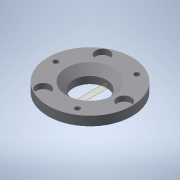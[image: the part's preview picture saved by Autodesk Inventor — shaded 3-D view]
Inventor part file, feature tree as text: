
AUTODESK INVENTOR PART (.ipt)
format: ipt  version: 2022 (Build 260153000, 153)  size: 187,392 bytes
history: native  units: mm
features: reference x5, sketch x4, extrude x2, other x2, plane x1, revolve x1, hole x1
ambient origin geometry x8: Origin, YZ Plane, XZ Plane, XY Plane, X Axis, Y Axis, Z Axis, Center Point
bodies: Volumenkörper1 (feature_tree)
feature tree (16):
  plane  "Arbeitsebene1"
  revolve  "Umdrehung1"
  hole  "Bohrung1"  [1 undecoded]
  extrude  "Extrusion1"  Depth=4.0mm
  extrude  "Extrusion2"  Depth=1.3mm
  sketch  "Skizze1"  dims[d0=3.0mm d1=12.0mm]
  reference  "Referenz1"
  reference  "Referenz2"
  sketch  "Skizze2"  dims[d4=4.0mm d5=4.0mm]
  reference  "Referenz3"
  reference  "Referenz4"
  reference  "Referenz5"
  sketch  "Skizze3"  dims[d6=1.0mm d7=1.3mm]
  sketch  "Skizze4"  dims[d8=2.6mm d9=90.0deg d10=4.0mm d11=0.2mm d13=2.9mm d14=6.0mm d15=6.0mm d16=3.0mm d17=90.0deg d18=12.0mm d19=20.594885mm d20=0.0mm d21=8.0mm d22=8.0mm d23=8.0mm d24=3.0mm d25=0.0mm d26=0.5mm d27=0.0mm]
  other  "SMLM_Holder_v1.iam"
  other  "02_SMLM_Holdre_Bottom:1"
note: 1 required parameter value undecoded (feature->parameter linkage not recoverable at this tier; creation-order binding heuristic only, values carry confidence <= 0.55)
